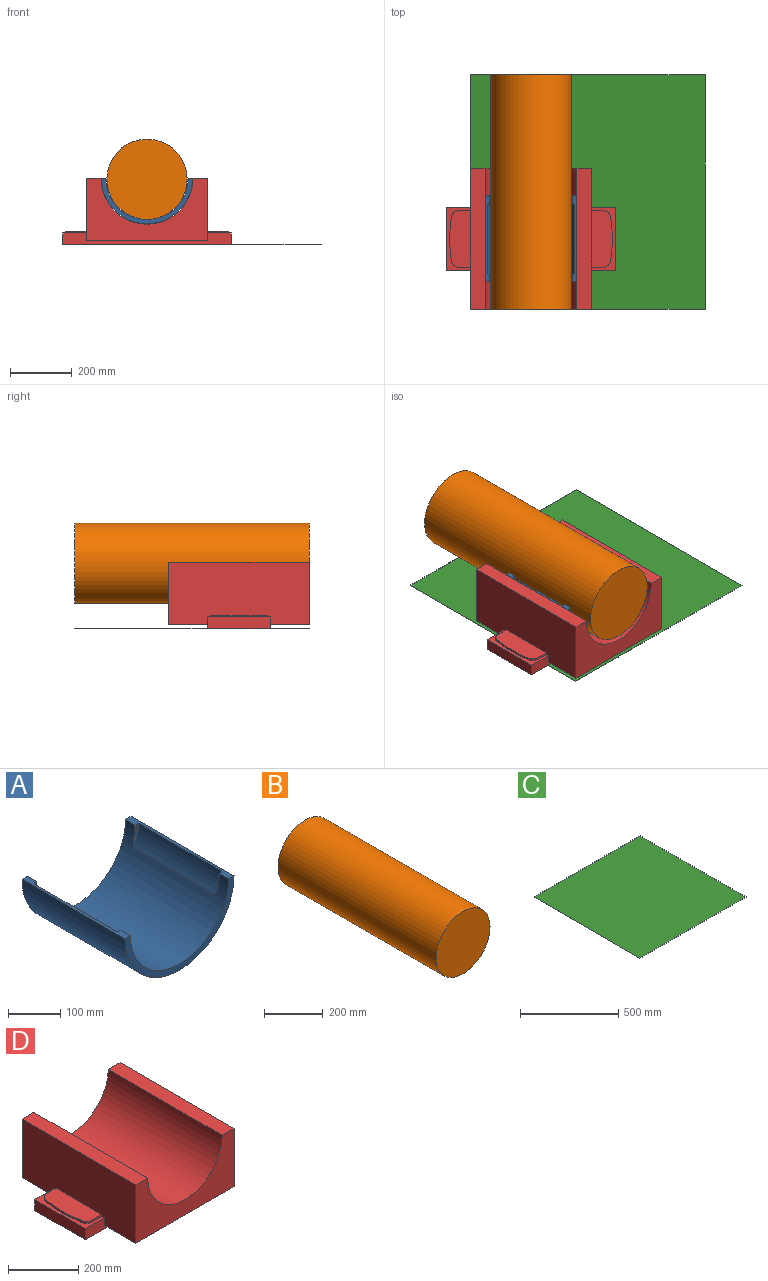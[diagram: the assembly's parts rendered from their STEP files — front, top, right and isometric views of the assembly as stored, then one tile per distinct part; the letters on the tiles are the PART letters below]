
ASSEMBLY  parts=4 mates=2
PART A: 16 faces, bbox 296.6x279.8x148.6 mm
  f0: plane 279.81x14.76mm, normal (0,0,1), area 2099.1mm2, adj f1,f2,f4,f5,f9,f10,f11,f14
  f1: cylinder r=133.53mm len=279.81mm, axis (0,-1,0), area 95204.3mm2, adj f0,f3,f4,f5,f6,f7,f8,f9
  f2: cylinder r=148.28mm len=296.57mm, axis (0,-1,0), area 130346.9mm2, adj f0,f3,f4,f5
  f3: plane 279.81x14.76mm, normal (0,0,1), area 2099.1mm2, adj f1,f2,f4,f5,f6,f7,f8,f12
  f4: plane 296.57x148.28mm, normal (0,1,0), area 6532mm2, adj f0,f1,f2,f3
  f5: plane 296.57x148.28mm, normal (0,-1,0), area 6532mm2, adj f0,f1,f2,f3
  f6: cylinder r=96.16mm len=222.66mm, axis (0,-1,0), area 11422.6mm2, adj f1,f3,f12,f13
  f7: plane 34.84x10.35mm, normal (0,-1,0), area 115.9mm2, adj f1,f3,f13
  f8: plane 34.84x10.35mm, normal (0,1,0), area 115.9mm2, adj f1,f3,f12
  f9: cylinder r=96.16mm len=222.66mm, axis (0,-1,0), area 11422.6mm2, adj f0,f1,f14,f15
  f10: plane 34.84x10.35mm, normal (0,-1,0), area 115.9mm2, adj f0,f1,f15
  f11: plane 34.84x10.35mm, normal (0,1,0), area 115.9mm2, adj f0,f1,f14
  f12: cone r=96.16mm half-angle=45deg, axis (0,1,0), area 197.9mm2, adj f1,f3,f6,f8
  f13: cone r=92.99mm half-angle=45deg, axis (0,-1,0), area 197.9mm2, adj f1,f3,f6,f7
  f14: cone r=92.99mm half-angle=45deg, axis (0,1,0), area 197.9mm2, adj f0,f1,f9,f11
  f15: cone r=96.16mm half-angle=45deg, axis (0,-1,0), area 197.9mm2, adj f0,f1,f9,f10
PART B: 3 faces, bbox 260.4x762x260.4 mm
  f0: cylinder r=130.18mm len=762mm, axis (0,1,0), area 623250.2mm2, adj f1,f2
  f1: plane 260.35x260.35mm, normal (0,-1,0), area 53236mm2, adj f0
  f2: plane 260.35x260.35mm, normal (0,1,0), area 53236mm2, adj f0
PART C: 6 faces, bbox 762x762x0.3 mm
  f0: plane 762x0.25mm, normal (0,1,0), area 193.5mm2, adj f1,f3,f4,f5
  f1: plane 762x0.25mm, normal (-1,0,0), area 193.5mm2, adj f0,f2,f4,f5
  f2: plane 762x0.25mm, normal (0,-1,0), area 193.5mm2, adj f1,f3,f4,f5
  f3: plane 762x0.25mm, normal (1,0,0), area 193.5mm2, adj f0,f2,f4,f5
  f4: plane 762x762mm, normal (0,0,1), area 580644mm2, adj f0,f1,f2,f3
  f5: plane 762x762mm, normal (0,0,-1), area 580644mm2, adj f0,f1,f2,f3
PART D: 28 faces, bbox 546.1x457.6x215.9 mm
  f0: plane 546.1x203.2mm, normal (0,0,-1), area 110967.5mm2, adj f6,f7,f8,f9
  f1: plane 457.61x47.63mm, normal (0,0,1), area 21793.5mm2, adj f2,f3,f22,f25
  f2: plane 393.7x203.2mm, normal (0,-1,0), area 45021.2mm2, adj f1,f22,f23,f24,f25,f27
  f3: plane 393.7x203.2mm, normal (0,1,0), area 45021.2mm2, adj f1,f22,f23,f24,f25,f26
  f4: plane 203.2x76.2mm, normal (0,0,1), area 3859.8mm2, adj f7,f8,f9,f16,f17,f18,f19,f20
  f5: plane 203.2x76.2mm, normal (0,0,1), area 3859.8mm2, adj f6,f8,f9,f10,f11,f12,f13,f14
  f6: plane 203.2x38.1mm, normal (-1,0,0), area 7741.9mm2, adj f0,f5,f8,f9
  f7: plane 203.2x38.1mm, normal (1,0,0), area 7741.9mm2, adj f0,f4,f8,f9
  f8: plane 546.1x38.1mm, normal (0,1,0), area 10806.4mm2, adj f0,f4,f5,f6,f7,f22,f23,f26
  f9: plane 546.1x38.1mm, normal (0,-1,0), area 10806.4mm2, adj f0,f4,f5,f6,f7,f22,f23,f27
  f10: cylinder r=25.4mm len=25.4mm, axis (0,0,-1), area 253.4mm2, adj f5,f11,f14,f15
  f11: cylinder r=457.2mm len=133.35mm, axis (0,0,-1), area 849.8mm2, adj f5,f10,f12,f15
  f12: cylinder r=25.4mm len=25.4mm, axis (0,0,-1), area 253.4mm2, adj f5,f11,f13,f15
  f13: plane 36.86x6.35mm, normal (0,-1,0), area 234.1mm2, adj f5,f12,f15,f22
  f14: plane 36.86x6.35mm, normal (0,1,0), area 234.1mm2, adj f5,f10,f15,f22
  f15: plane 184.15x67.15mm, normal (0,0,1), area 11624mm2, adj f10,f11,f12,f13,f14,f22
  f16: cylinder r=25.4mm len=25.4mm, axis (0,0,-1), area 253.4mm2, adj f4,f17,f20,f21
  f17: cylinder r=457.2mm len=133.35mm, axis (0,0,-1), area 849.8mm2, adj f4,f16,f18,f21
  f18: cylinder r=25.4mm len=25.4mm, axis (0,0,-1), area 253.4mm2, adj f4,f17,f19,f21
  f19: plane 36.86x6.35mm, normal (0,1,0), area 234.1mm2, adj f4,f18,f21,f23
  f20: plane 36.86x6.35mm, normal (0,-1,0), area 234.1mm2, adj f4,f16,f21,f23
  f21: plane 184.15x67.15mm, normal (0,0,1), area 11624mm2, adj f16,f17,f18,f19,f20,f23
  f22: plane 457.61x203.2mm, normal (-1,0,0), area 86655mm2, adj f1,f2,f3,f5,f8,f9,f13,f14
  f23: plane 457.61x203.2mm, normal (1,0,0), area 86655mm2, adj f2,f3,f4,f8,f9,f19,f20,f21
  f24: plane 457.61x47.63mm, normal (0,0,1), area 21793.5mm2, adj f2,f3,f23,f25
  f25: cylinder r=149.22mm len=457.61mm, axis (0,1,0), area 214527.8mm2, adj f1,f2,f3,f24
  f26: plane 393.7x127.2mm, normal (0,0,-1), area 50079.9mm2, adj f3,f8,f22,f23
  f27: plane 393.7x127.2mm, normal (0,0,-1), area 50079.9mm2, adj f2,f9,f22,f23
PLACE A t=(53.72,-2.39,482.51)mm
PLACE B t=(53.72,670.71,479.21)mm
PLACE C t=(233.89,221.76,266.36)mm fixed
PLACE D t=(53.72,35.91,266.61)mm
MATE fastened C.f2 <-> B.f1  axis (0,-1,0) through (-143.13,-91.29,266.61)mm
MATE fastened A.f1 <-> D.f25  axis (0,-1,0) through (53.72,-2.39,482.51)mm
